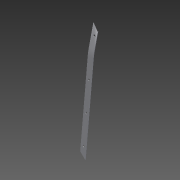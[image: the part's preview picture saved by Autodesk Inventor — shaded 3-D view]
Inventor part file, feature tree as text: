
AUTODESK INVENTOR PART (.ipt)
format: ipt  version: 2015 (Build 190159000, 159)  size: 139,776 bytes
history: native  units: mm
features: reference x9, sketch x6, other x3, extrude x2, sweep x1, hole x1
ambient origin geometry x8: Origin, YZ Plane, XZ Plane, XY Plane, X Axis, Y Axis, Z Axis, Center Point
bodies: Body1 (feature_tree)
feature tree (22):
  other  "Listwa_siedziska_prawa"
  sweep  "Przeciągnięcie1"
  sketch  "Szkic2"
  other  "Gięcie części1"
  extrude  "Wyciągnięcie proste3"  Depth=1.5mm
  extrude  "Wyciągnięcie proste4"  Depth=1.22173mm
  hole  "Otwór2"  [1 undecoded]
  sketch  "Szkic1"
  sketch  "Szkic4"
  sketch  "Szkic5"
  other  "Bryła2"
  sketch  "Szkic6"
  reference  "Odniesienie1"
  sketch  "Szkic7"
  reference  "Odniesienie2"
  reference  "Odniesienie3"
  reference  "Odniesienie4"
  reference  "Odniesienie5"
  reference  "Odniesienie6"
  reference  "Odniesienie7"
  reference  "Odniesienie8"
  reference  "Odniesienie9"
note: 1 required parameter value undecoded (feature->parameter linkage not recoverable at this tier; creation-order binding heuristic only, values carry confidence <= 0.55)
